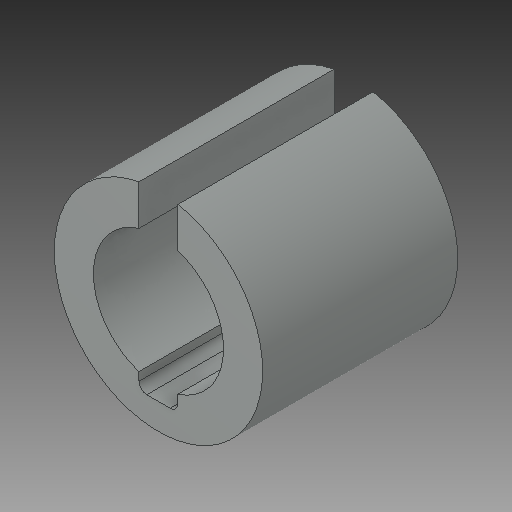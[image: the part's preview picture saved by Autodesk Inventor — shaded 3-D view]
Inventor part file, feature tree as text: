
AUTODESK INVENTOR PART (.ipt)
format: ipt  version: 2018 (Build 220112000, 112)  size: 116,224 bytes
history: native  units: in
note: dims shown in document units (in); Inventor stores cm internally (conversion verified against a paired STEP export)
features: fillet x1
ambient origin geometry x8: Origin, YZ Plane, XZ Plane, XY Plane, X Axis, Y Axis, Z Axis, Center Point
bodies: Solid1 (feature_tree)
feature tree (1):
  fillet  "Fillet1"  [1 undecoded]
note: 1 required parameter value undecoded (feature->parameter linkage not recoverable at this tier; creation-order binding heuristic only, values carry confidence <= 0.55)
